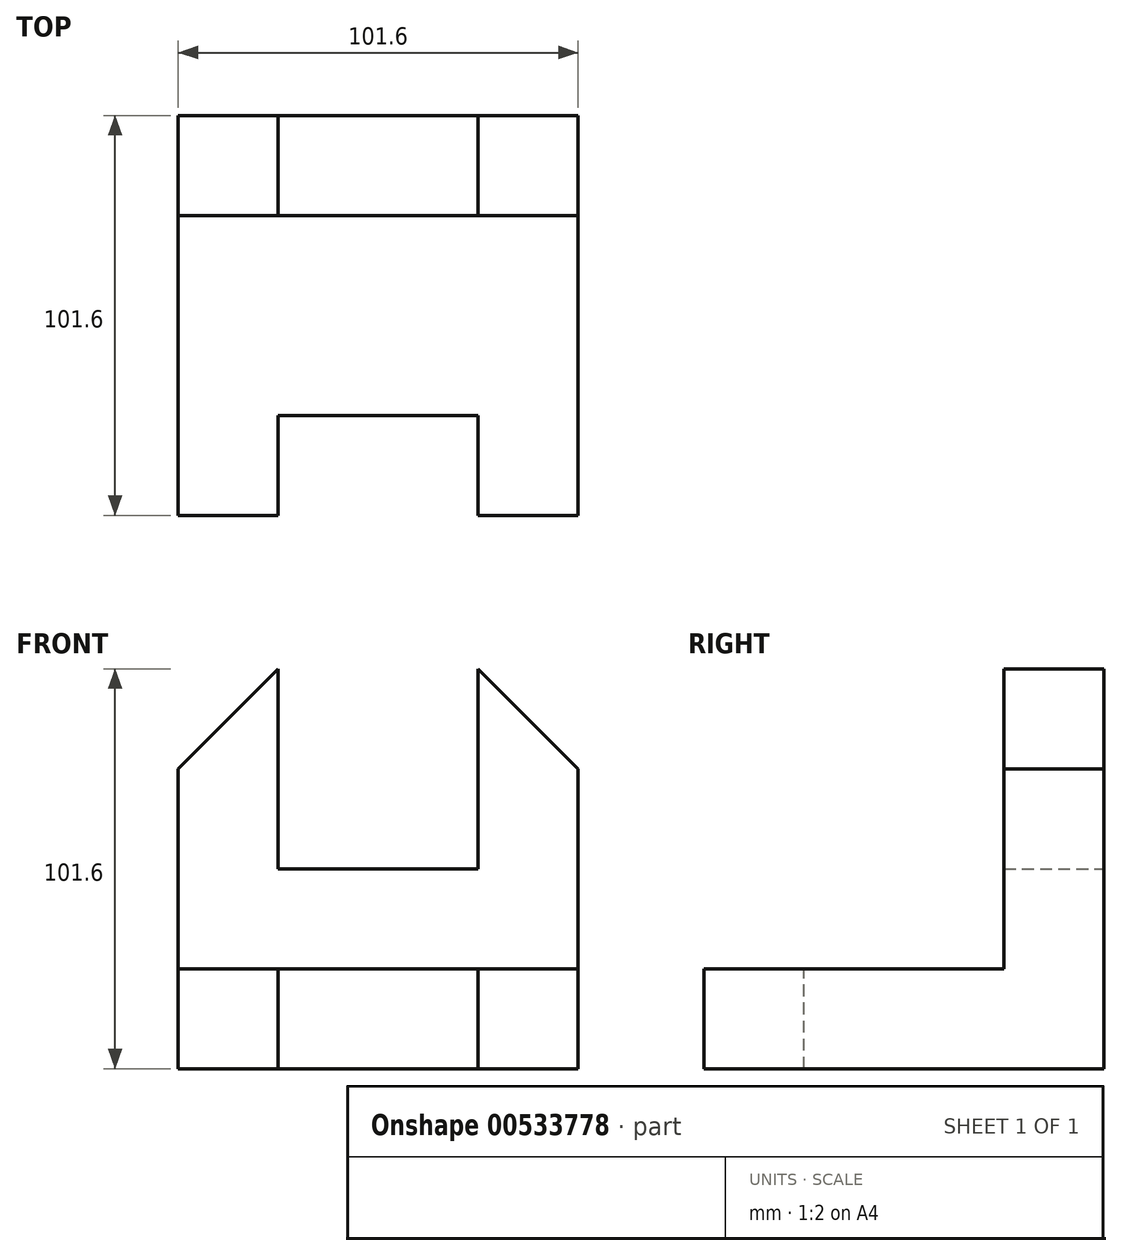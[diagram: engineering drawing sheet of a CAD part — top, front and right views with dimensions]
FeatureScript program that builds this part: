
annotation { "Feature Type Name" : "Feature", "Feature Type Description" : "" }
export const myFeature = defineFeature(function(context is Context, id is Id, definition is map)
    precondition{}
    {
        {
            var Q0;
            Q0=qCreatedBy(makeId("Front.planeOp"),FACE);
            var sketch = newSketch(context, id + "F0", { "sketchPlane" : qUnion([Q0])});
            skLineSegment(sketch, "E0", {"start": v(-58.59, 39.04) * mm, "end": v(-58.59, -37.16) * mm});
            skLineSegment(sketch, "E1", {"start": v(-58.59, -37.16) * mm, "end": v(43.01, -37.16) * mm});
            skLineSegment(sketch, "E2", {"start": v(43.01, -37.16) * mm, "end": v(43.01, 39.04) * mm});
            skLineSegment(sketch, "E3", {"start": v(-33.19, 64.44) * mm, "end": v(-58.59, 39.04) * mm});
            skLineSegment(sketch, "E4", {"start": v(-33.19, 64.44) * mm, "end": v(-33.19, 13.64) * mm});
            skLineSegment(sketch, "E5", {"start": v(-33.19, 13.64) * mm, "end": v(17.61, 13.64) * mm});
            skLineSegment(sketch, "E6", {"start": v(17.61, 13.64) * mm, "end": v(17.61, 64.44) * mm});
            skLineSegment(sketch, "E7", {"start": v(17.61, 64.44) * mm, "end": v(43.01, 39.04) * mm});
            skSolve(sketch);
        }
        {
            var Q0;
            Q0=makeQuery(id+"F0.imprint","IMPRINT",FACE,{"disambiguationData":[TD([[makeQuery(id+"F0.imprint","IMPRINT",EDGE,{"derivedFrom":sQuery(id+"F0.wireOp",EDGE,"E0")}),1.0]])]});
            extrude(context, id + "F1", {"entities" : qUnion([Q0]), "depth" : 25.4 * mm, "offsetDistance" : 25.4 * mm});
        }
        {
            var Q0;
            Q0=makeQuery(id+"F1.opExtrude","CAP_FACE",FACE,{"disambiguationData":[OSD([sQuery(id+"F0.wireOp",EDGE,"E0"),sQuery(id+"F0.wireOp",EDGE,"E1"),sQuery(id+"F0.wireOp",EDGE,"E2"),sQuery(id+"F0.wireOp",EDGE,"E3"),sQuery(id+"F0.wireOp",EDGE,"E4"),sQuery(id+"F0.wireOp",EDGE,"E5"),sQuery(id+"F0.wireOp",EDGE,"E6"),sQuery(id+"F0.wireOp",EDGE,"E7")])],"isStart":false});
            var sketch = newSketch(context, id + "F2", { "sketchPlane" : qUnion([Q0])});
            skLineSegment(sketch, "E8.bottom", {"start": v(-58.59, -37.16) * mm, "end": v(43.01, -37.16) * mm});
            skLineSegment(sketch, "E8.top", {"start": v(-58.59, -11.76) * mm, "end": v(43.01, -11.76) * mm});
            skLineSegment(sketch, "E8.left", {"start": v(-58.59, -37.16) * mm, "end": v(-58.59, -11.76) * mm});
            skLineSegment(sketch, "E8.right", {"start": v(43.01, -37.16) * mm, "end": v(43.01, -11.76) * mm});
            skSolve(sketch);
        }
        {
            var Q0;
            Q0=makeQuery(id+"F2.imprint","IMPRINT",FACE,{"disambiguationData":[TD([[makeQuery(id+"F2.imprint","IMPRINT",EDGE,{"derivedFrom":sQuery(id+"F2.wireOp",EDGE,"E8.bottom")}),1.0]])]});
            extrude(context, id + "F3", {"entities" : qUnion([Q0]), "operationType" : NewBodyOperationType.ADD, "depth" : 76.2 * mm, "offsetDistance" : 25.4 * mm});
        }
        {
            var Q0;
            Q0=makeQuery(id+"F3.opExtrude","SWEPT_FACE",FACE,{"disambiguationData":[OSD([sQuery(id+"F2.wireOp",EDGE,"E8.top")])]});
            var sketch = newSketch(context, id + "F4", { "sketchPlane" : qUnion([Q0])});
            skLineSegment(sketch, "E9.bottom", {"start": v(-33.19, -101.6) * mm, "end": v(17.61, -101.6) * mm});
            skLineSegment(sketch, "E9.top", {"start": v(-33.19, -76.2) * mm, "end": v(17.61, -76.2) * mm});
            skLineSegment(sketch, "E9.left", {"start": v(-33.19, -101.6) * mm, "end": v(-33.19, -76.2) * mm});
            skLineSegment(sketch, "E9.right", {"start": v(17.61, -101.6) * mm, "end": v(17.61, -76.2) * mm});
            skSolve(sketch);
        }
        {
            var Q0;
            Q0=makeQuery(id+"F4.imprint","IMPRINT",FACE,{"disambiguationData":[TD([[makeQuery(id+"F4.imprint","IMPRINT",EDGE,{"derivedFrom":sQuery(id+"F4.wireOp",EDGE,"E9.bottom")}),1.0]])]});
            extrude(context, id + "F5", {"entities" : qUnion([Q0]), "operationType" : NewBodyOperationType.REMOVE, "oppositeDirection" : true, "depth" : 25.4 * mm, "offsetDistance" : 25.4 * mm});
        }
    });
